# Revit family: The Peckham Book Throne
name_source: partatom
category: Plumbing Fixtures
revit_build: Autodesk Revit Architecture 2014 (Build: 20130308_1515(x64)
units: mm (PartAtom-declared; Revit-internal decimal feet)

## types (7) — shared parameters
Book1 = <By Category>
Book2 = <By Category>
Book3 = <By Category>
Book4 = <By Category>
Book5 = <By Category>
Shower Base = Laminate - Linen,Matte
fabric = <By Category>

## per-type parameters (varying)
| type | Assembly Code | Depth | Width |
| 36" x 36" | D2010710 | 914 mm | 1486 mm  [stored 4.87533 ft] |
| 32" x 32" | D2010710 | 813 mm | 813 mm |
| 48" x 34" | D2010710 | 864 mm | 1219 mm |
| 810 x 810mm |  | 813 mm | 813 mm |
| 910 x 910mm |  | 914 mm | 914 mm |
| 1220 x 860mm |  | 864 mm | 1219 mm |
| 1000x800 |  | 800 mm  [stored 2.62467 ft] | 1000 mm  [stored 3.28084 ft] |

note: [stored X ft] marks values corroborated as IEEE doubles in the binary element streams (Revit-internal decimal feet)

## geometry (parser evidence)
native form markers: Sweep x1
no freeform markers — native parametric forms only
